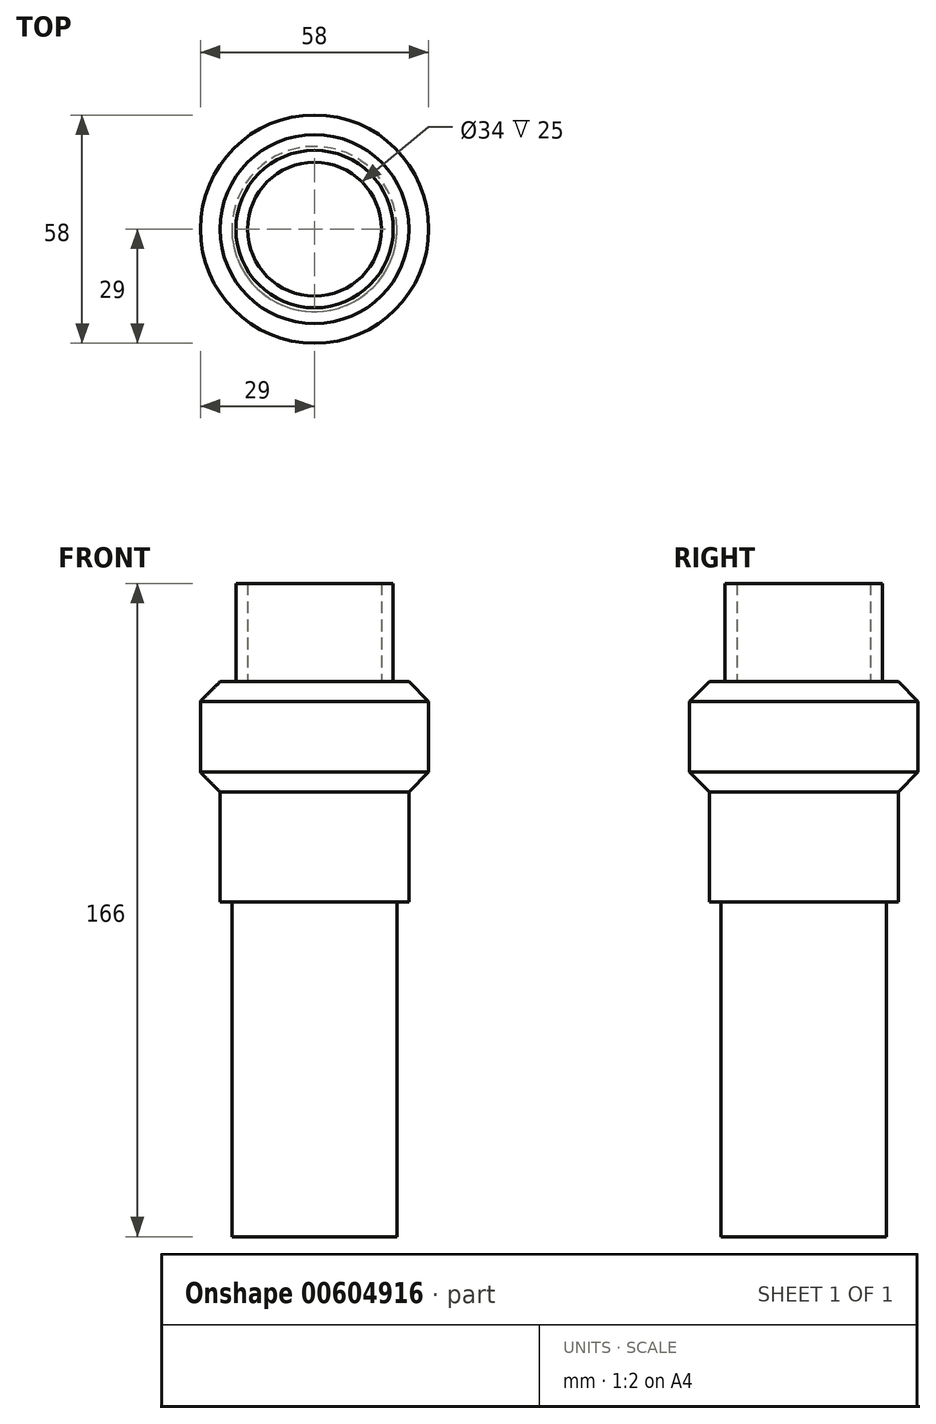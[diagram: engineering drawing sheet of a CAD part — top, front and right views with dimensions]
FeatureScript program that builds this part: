
annotation { "Feature Type Name" : "Feature", "Feature Type Description" : "" }
export const myFeature = defineFeature(function(context is Context, id is Id, definition is map)
    precondition{}
    {
        {
            var Q0;
            Q0=qCreatedBy(makeId("Top.planeOp"),FACE);
            var sketch = newSketch(context, id + "F0", { "sketchPlane" : qUnion([Q0])});
            skCircle(sketch, "E0", {"center": v(0, 0) * mm, "radius": 21 * mm});
            skSolve(sketch);
        }
        {
            var Q0;
            Q0=qSketchRegion(id+"F0",true);
            extrude(context, id + "F1", {"entities" : qUnion([Q0]), "depth" : 100 * mm, "offsetDistance" : 25 * mm});
        }
        {
            var Q0;
            Q0=qCreatedBy(makeId("Front.planeOp"),FACE);
            var sketch = newSketch(context, id + "F2", { "sketchPlane" : qUnion([Q0])});
            skLineSegment(sketch, "E1", {"start": v(0, 0) * mm, "end": v(0, 149.12) * mm, "construction": true});
            skLineSegment(sketch, "E2", {"start": v(0, 85) * mm, "end": v(-24, 85) * mm});
            skLineSegment(sketch, "E3", {"start": v(-24, 85) * mm, "end": v(-24, 113) * mm});
            skLineSegment(sketch, "E4", {"start": v(-24, 113) * mm, "end": v(-29, 118) * mm});
            skLineSegment(sketch, "E5", {"start": v(-29, 118) * mm, "end": v(-29, 136) * mm});
            skLineSegment(sketch, "E6", {"start": v(-29, 136) * mm, "end": v(-24, 141) * mm});
            skLineSegment(sketch, "E7", {"start": v(-24, 141) * mm, "end": v(0, 141) * mm});
            skLineSegment(sketch, "E8", {"start": v(0, 141) * mm, "end": v(0, 85) * mm});
            skSolve(sketch);
        }
        {
            var Q0;
            Q0=qSketchRegion(id+"F2",true);
            var Q1;
            Q1=sQuery(id+"F2.wireOp",EDGE,"E1");
            revolve(context, id + "F3", {"operationType" : NewBodyOperationType.ADD, "entities" : qUnion([Q0]), "axis" : qUnion([Q1]), "revolveType" : RevolveType.FULL});
        }
        {
            var Q0;
            Q0=makeQuery(id+"F3.opRevolve","SWEPT_FACE",FACE,{"disambiguationData":[OSD([sQuery(id+"F2.wireOp",EDGE,"E7")])]});
            var sketch = newSketch(context, id + "F4", { "sketchPlane" : qUnion([Q0])});
            skCircle(sketch, "E9", {"center": v(0, 0) * mm, "radius": 20 * mm});
            skCircle(sketch, "E10", {"center": v(0, 0) * mm, "radius": 17 * mm});
            skSolve(sketch);
        }
        {
            var Q0;
            Q0=qSketchRegion(id+"F4",true);
            extrude(context, id + "F5", {"entities" : qUnion([Q0]), "operationType" : NewBodyOperationType.ADD, "depth" : 25 * mm, "offsetDistance" : 25 * mm});
        }
    });
